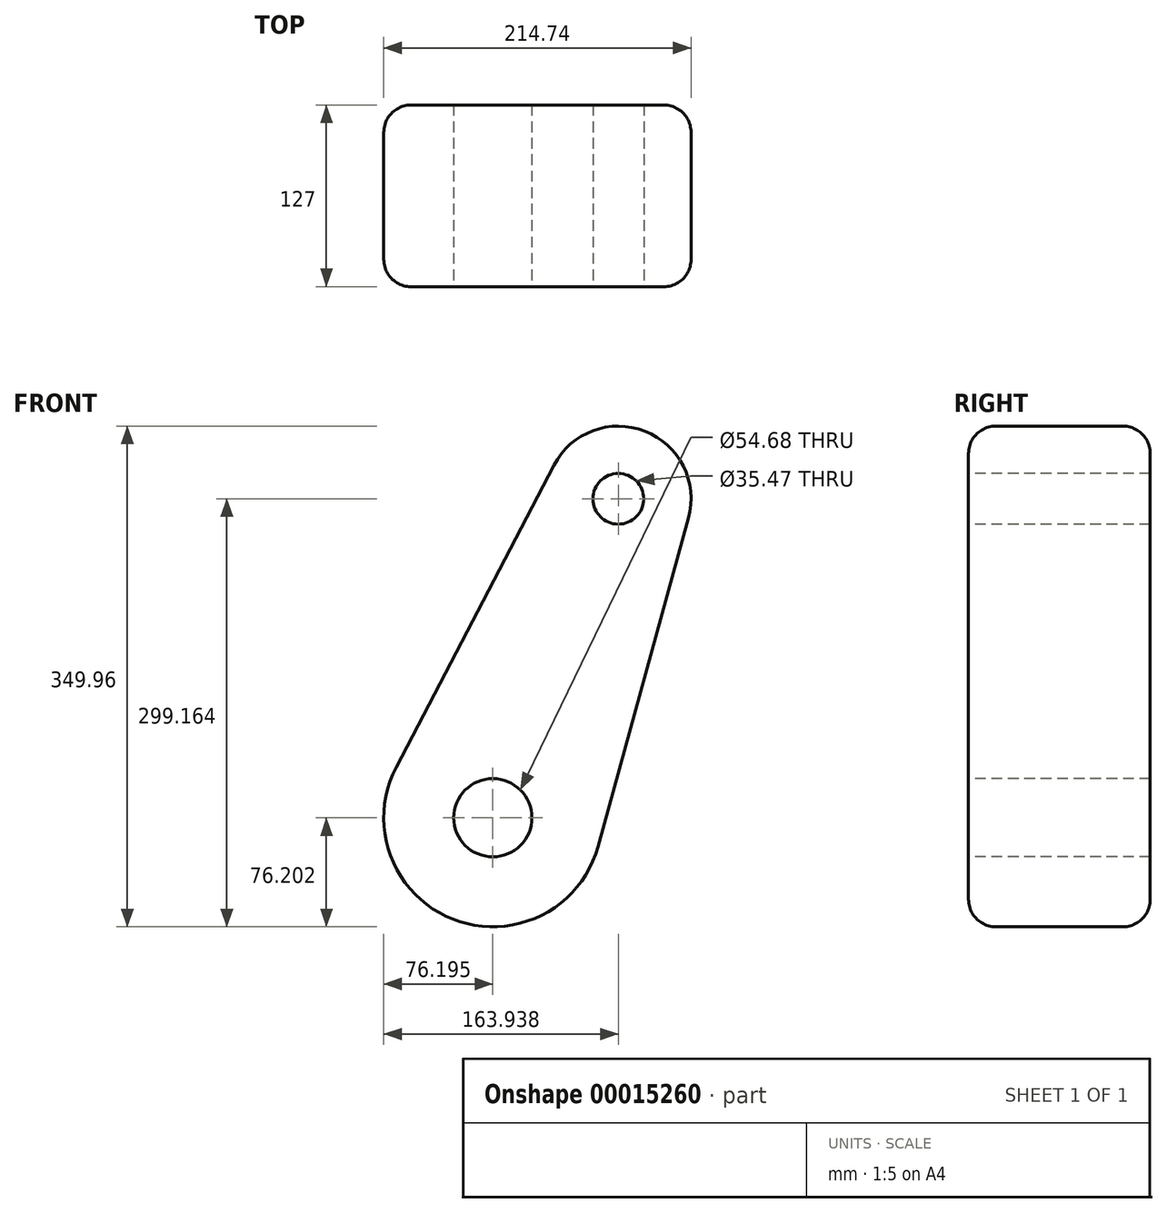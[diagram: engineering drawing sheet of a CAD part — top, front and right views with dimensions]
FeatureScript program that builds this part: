
annotation { "Feature Type Name" : "Feature", "Feature Type Description" : "" }
export const myFeature = defineFeature(function(context is Context, id is Id, definition is map)
    precondition{}
    {
        {
            var Q0;
            Q0=qCreatedBy(makeId("Front.planeOp"),FACE);
            var sketch = newSketch(context, id + "F0", { "sketchPlane" : qUnion([Q0])});
            skArc(sketch, "E0", {"start": v(-181.61, -116.9) * mm, "mid": v(-141.97, -223.07) * mm, "end": v(-40.6, -172.39) * mm});
            skCircle(sketch, "E1", {"center": v(-114.06, -152.16) * mm, "radius": 27.34 * mm});
            skCircle(sketch, "E2", {"center": v(-26.32, 70.8) * mm, "radius": 17.73 * mm});
            skArc(sketch, "E3", {"start": v(22.65, 57.32) * mm, "mid": v(-7.72, 118.08) * mm, "end": v(-71.36, 94.31) * mm});
            skLineSegment(sketch, "E4", {"start": v(-181.61, -116.9) * mm, "end": v(-71.36, 94.31) * mm});
            skLineSegment(sketch, "E5", {"start": v(-40.6, -172.39) * mm, "end": v(22.65, 57.32) * mm});
            skSolve(sketch);
        }
        {
            var Q0;
            Q0=makeQuery(id+"F0.imprint","IMPRINT",FACE,{"disambiguationData":[TD([[makeQuery(id+"F0.imprint","IMPRINT",EDGE,{"derivedFrom":sQuery(id+"F0.wireOp",EDGE,"E0")}),1.0]])]});
            extrude(context, id + "F1", {"entities" : qUnion([Q0]), "oppositeDirection" : true, "depth" : 127 * mm});
        }
        {
            var Q0;
            Q0=makeQuery(id+"F1.opExtrude","CAP_EDGE",EDGE,{"disambiguationData":[OSD([sQuery(id+"F0.wireOp",EDGE,"E4")])],"isStart":true});
            var Q1;
            Q1=makeQuery(id+"F1.opExtrude","CAP_EDGE",EDGE,{"disambiguationData":[OSD([sQuery(id+"F0.wireOp",EDGE,"E3")])],"isStart":true});
            var Q2;
            Q2=makeQuery(id+"F1.opExtrude","CAP_EDGE",EDGE,{"disambiguationData":[OSD([sQuery(id+"F0.wireOp",EDGE,"E5")])],"isStart":true});
            var Q3;
            Q3=makeQuery(id+"F1.opExtrude","CAP_EDGE",EDGE,{"disambiguationData":[OSD([sQuery(id+"F0.wireOp",EDGE,"E0")])],"isStart":true});
            var Q4;
            Q4=makeQuery(id+"F1.opExtrude","CAP_EDGE",EDGE,{"disambiguationData":[OSD([sQuery(id+"F0.wireOp",EDGE,"E4")])],"isStart":false});
            fillet(context, id + "F2", {"entities" : qUnion([Q0, Q1, Q2, Q3, Q4]), "radius" : 19.05 * mm, "tangentPropagation" : true, "allowEdgeOverflow" : false});
        }
        {
            var Q0;
            Q0=makeQuery(id+"F1.opExtrude","CAP_FACE",FACE,{"disambiguationData":[OSD([sQuery(id+"F0.wireOp",EDGE,"E0"),sQuery(id+"F0.wireOp",EDGE,"E1"),sQuery(id+"F0.wireOp",EDGE,"E2"),sQuery(id+"F0.wireOp",EDGE,"E3"),sQuery(id+"F0.wireOp",EDGE,"E4"),sQuery(id+"F0.wireOp",EDGE,"E5")])],"isStart":true});
            var sketch = newSketch(context, id + "F3", { "sketchPlane" : qUnion([Q0])});
            skCircle(sketch, "E6", {"center": v(-72.1, -50.92) * mm, "radius": 25.67 * mm});
            skSolve(sketch);
        }
        {
            var Q0;
            Q0=makeQuery(id+"F3.imprint","IMPRINT",FACE,{"disambiguationData":[TD([[makeQuery(id+"F3.imprint","IMPRINT",EDGE,{"derivedFrom":sQuery(id+"F3.wireOp",EDGE,"E6")}),1.0]])]});
            extrude(context, id + "F4", {"entities" : qUnion([Q0]), "operationType" : NewBodyOperationType.ADD, "oppositeDirection" : true, "depth" : 25.4 * mm});
        }
    });
